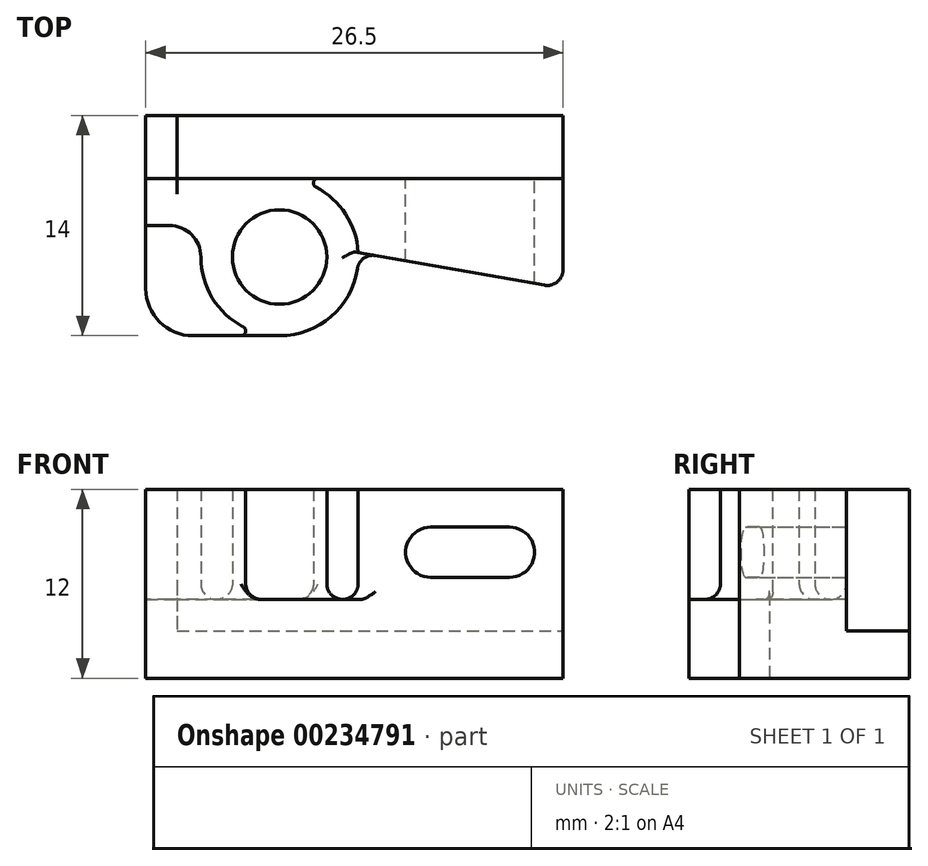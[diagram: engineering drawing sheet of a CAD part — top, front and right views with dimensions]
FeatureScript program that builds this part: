
annotation { "Feature Type Name" : "Feature", "Feature Type Description" : "" }
export const myFeature = defineFeature(function(context is Context, id is Id, definition is map)
    precondition{}
    {
        {
            var Q0;
            Q0=qCreatedBy(makeId("Top.planeOp"),FACE);
            var sketch = newSketch(context, id + "F0", { "sketchPlane" : qUnion([Q0])});
            skLineSegment(sketch, "E0", {"start": v(0, 5) * mm, "end": v(18, 5) * mm});
            skLineSegment(sketch, "E1", {"start": v(18, 5) * mm, "end": v(18, -2) * mm});
            skLineSegment(sketch, "E2", {"start": v(18, -2) * mm, "end": v(5, 0.3) * mm});
            skLineSegment(sketch, "E3", {"start": v(0, -5) * mm, "end": v(-5.5, -5) * mm});
            skLineSegment(sketch, "E4", {"start": v(-8.5, -2) * mm, "end": v(-8.5, 2) * mm});
            skLineSegment(sketch, "E5", {"start": v(-8.5, 2) * mm, "end": v(-7, 2) * mm});
            skCircle(sketch, "E6", {"center": v(0, 0) * mm, "radius": 3 * mm});
            skLineSegment(sketch, "E7", {"start": v(-8.5, 2) * mm, "end": v(-8.5, 9) * mm});
            skLineSegment(sketch, "E8", {"start": v(-8.5, 9) * mm, "end": v(18, 9) * mm});
            skLineSegment(sketch, "E9", {"start": v(18, 9) * mm, "end": v(18, 5) * mm});
            skLineSegment(sketch, "E10", {"start": v(0, 5) * mm, "end": v(-8.5, 5) * mm});
            skPoint(sketch, "E11.visualSharp", {"position": v(-8.5, -5) * mm});
            skArc(sketch, "E11.filletArc", {"start": v(-8.5, -2) * mm, "mid": v(-7.62, -4.12) * mm, "end": v(-5.5, -5) * mm});
            skArc(sketch, "E12", {"start": v(-5, 0) * mm, "mid": v(3.54, -3.54) * mm, "end": v(0, 5) * mm});
            skPoint(sketch, "E13.visualSharp", {"position": v(-4.58, 2) * mm});
            skArc(sketch, "E13.filletArc", {"start": v(-5, 0) * mm, "mid": v(-5.59, 1.41) * mm, "end": v(-7, 2) * mm});
            skLineSegment(sketch, "E14", {"start": v(-6.5, 5) * mm, "end": v(-6.5, 9) * mm});
            skSolve(sketch);
        }
        {
            var Q0;
            Q0=makeQuery(id+"F0.imprint","IMPRINT",FACE,{"disambiguationData":[TD([[makeQuery(id+"F0.imprint","IMPRINT",EDGE,{"derivedFrom":sQuery(id+"F0.wireOp",EDGE,"E0")}),1.0]])]});
            var Q1;
            {var subQ2=sQuery(id+"F0.wireOp",EDGE,"E5");Q1=makeQuery(id+"F0.imprint","IMPRINT",FACE,{"disambiguationData":[TD([[makeQuery(id+"F0.imprint","IMPRINT",EDGE,{"derivedFrom":subQ2}),1.0]])]});}
            var Q2;
            {var subQ0=sQuery(id+"F0.wireOp",EDGE,"E0");Q2=makeQuery(id+"F0.imprint","IMPRINT",FACE,{"disambiguationData":[TD([[makeQuery(id+"F0.imprint","IMPRINT",EDGE,{"derivedFrom":subQ0}),-1.0]])]});}
            var Q3;
            Q3=makeQuery(id+"F0.imprint","IMPRINT",FACE,{"disambiguationData":[TD([[makeQuery(id+"F0.imprint","IMPRINT",EDGE,{"derivedFrom":sQuery(id+"F0.wireOp",EDGE,"E6")}),1.0]])]});
            var Q4;
            {var subQ1=sQuery(id+"F0.wireOp",EDGE,"E3");Q4=makeQuery(id+"F0.imprint","IMPRINT",FACE,{"disambiguationData":[TD([[makeQuery(id+"F0.imprint","IMPRINT",EDGE,{"derivedFrom":subQ1}),-1.0]])]});}
            var Q5;
            {var subQ5=sQuery(id+"F0.wireOp",EDGE,"E14");Q5=makeQuery(id+"F0.imprint","IMPRINT",FACE,{"disambiguationData":[TD([[makeQuery(id+"F0.imprint","IMPRINT",EDGE,{"derivedFrom":subQ5}),1.0]])]});}
            extrude(context, id + "F1", {"entities" : qUnion([Q0, Q1, Q2, Q3, Q4, Q5]), "depth" : 3 * mm});
        }
        {
            var Q0;
            {var subQ0=sQuery(id+"F0.wireOp",EDGE,"E0");Q0=makeQuery(id+"F0.imprint","IMPRINT",FACE,{"disambiguationData":[TD([[makeQuery(id+"F0.imprint","IMPRINT",EDGE,{"derivedFrom":subQ0}),-1.0]])]});}
            var Q1;
            Q1=makeQuery(id+"F0.imprint","IMPRINT",FACE,{"disambiguationData":[TD([[makeQuery(id+"F0.imprint","IMPRINT",EDGE,{"derivedFrom":sQuery(id+"F0.wireOp",EDGE,"E6")}),1.0]])]});
            var Q2;
            {var subQ1=sQuery(id+"F0.wireOp",EDGE,"E3");Q2=makeQuery(id+"F0.imprint","IMPRINT",FACE,{"disambiguationData":[TD([[makeQuery(id+"F0.imprint","IMPRINT",EDGE,{"derivedFrom":subQ1}),-1.0]])]});}
            var Q3;
            {var subQ2=sQuery(id+"F0.wireOp",EDGE,"E5");Q3=makeQuery(id+"F0.imprint","IMPRINT",FACE,{"disambiguationData":[TD([[makeQuery(id+"F0.imprint","IMPRINT",EDGE,{"derivedFrom":subQ2}),1.0]])]});}
            var Q4;
            {var subQ5=sQuery(id+"F0.wireOp",EDGE,"E14");Q4=makeQuery(id+"F0.imprint","IMPRINT",FACE,{"disambiguationData":[TD([[makeQuery(id+"F0.imprint","IMPRINT",EDGE,{"derivedFrom":subQ5}),1.0]])]});}
            extrude(context, id + "F2", {"entities" : qUnion([Q0, Q1, Q2, Q3, Q4]), "operationType" : NewBodyOperationType.ADD, "depth" : 5 * mm});
        }
        {
            var Q0;
            {var subQ0=sQuery(id+"F0.wireOp",EDGE,"E0");Q0=makeQuery(id+"F0.imprint","IMPRINT",FACE,{"disambiguationData":[TD([[makeQuery(id+"F0.imprint","IMPRINT",EDGE,{"derivedFrom":subQ0}),-1.0]])]});}
            var Q1;
            Q1=makeQuery(id+"F0.imprint","IMPRINT",FACE,{"disambiguationData":[TD([[makeQuery(id+"F0.imprint","IMPRINT",EDGE,{"derivedFrom":sQuery(id+"F0.wireOp",EDGE,"E6")}),1.0]])]});
            var Q2;
            {var subQ1=sQuery(id+"F0.wireOp",EDGE,"E3");Q2=makeQuery(id+"F0.imprint","IMPRINT",FACE,{"disambiguationData":[TD([[makeQuery(id+"F0.imprint","IMPRINT",EDGE,{"derivedFrom":subQ1}),-1.0]])]});}
            var Q3;
            {var subQ5=sQuery(id+"F0.wireOp",EDGE,"E14");Q3=makeQuery(id+"F0.imprint","IMPRINT",FACE,{"disambiguationData":[TD([[makeQuery(id+"F0.imprint","IMPRINT",EDGE,{"derivedFrom":subQ5}),1.0]])]});}
            extrude(context, id + "F3", {"entities" : qUnion([Q0, Q1, Q2, Q3]), "operationType" : NewBodyOperationType.ADD, "depth" : 12 * mm});
        }
        {
            var Q0;
            Q0=makeQuery(id+"F3.opExtrude","SWEPT_EDGE",EDGE,{"disambiguationData":[OSD([sQuery(id+"F0.wireOp",EDGE,"E0"),sQuery(id+"F0.wireOp",EDGE,"E10"),sQuery(id+"F0.wireOp",EDGE,"E12")])]});
            var Q1;
            Q1=makeQuery(id+"F3.opExtrude","SWEPT_EDGE",EDGE,{"disambiguationData":[OSD([sQuery(id+"F0.wireOp",EDGE,"E3"),sQuery(id+"F0.wireOp",EDGE,"E12")])]});
            fillet(context, id + "F4", {"entities" : qUnion([Q0, Q1]), "radius" : 0.3 * mm, "tangentPropagation" : true, "allowEdgeOverflow" : false});
        }
        {
            var Q0;
            Q0=makeQuery(id+"F3.boolean.opBoolean","INTERSECT",EDGE,{"derivedFrom":[makeQuery(id+"F2.opExtrude","CAP_FACE",FACE,{"disambiguationData":[OSD([sQuery(id+"F0.wireOp",EDGE,"E0"),sQuery(id+"F0.wireOp",EDGE,"E1"),sQuery(id+"F0.wireOp",EDGE,"E2"),sQuery(id+"F0.wireOp",EDGE,"E3"),sQuery(id+"F0.wireOp",EDGE,"E4"),sQuery(id+"F0.wireOp",EDGE,"E7"),sQuery(id+"F0.wireOp",EDGE,"E10"),sQuery(id+"F0.wireOp",EDGE,"E11.filletArc"),sQuery(id+"F0.wireOp",EDGE,"E12")])],"isStart":false}),makeQuery(id+"F3.opExtrude","SWEPT_FACE",FACE,{"disambiguationData":[OSD([sQuery(id+"F0.wireOp",EDGE,"E6")])]})]});
            var Q1;
            {var subQ0=sQuery(id+"F0.wireOp",EDGE,"E12");var subQ1=sQuery(id+"F0.wireOp",EDGE,"E3");Q1=makeQuery(id+"F3.boolean.opBoolean","INTERSECT",EDGE,{"derivedFrom":[makeQuery(id+"F2.opExtrude","CAP_FACE",FACE,{"disambiguationData":[OSD([sQuery(id+"F0.wireOp",EDGE,"E0"),sQuery(id+"F0.wireOp",EDGE,"E1"),sQuery(id+"F0.wireOp",EDGE,"E2"),subQ1,sQuery(id+"F0.wireOp",EDGE,"E4"),sQuery(id+"F0.wireOp",EDGE,"E7"),sQuery(id+"F0.wireOp",EDGE,"E10"),sQuery(id+"F0.wireOp",EDGE,"E11.filletArc"),subQ0])],"isStart":false}),makeQuery(id+"F3.opExtrude","SWEPT_FACE",FACE,{"disambiguationData":[OSD([subQ0]),TDD([makeQuery(id+"F0.imprint","IMPRINT",EDGE,{"disambiguationData":[TD([[makeQuery(id+"F0.imprint","INTERSECT",VERTEX,{"derivedFrom":[subQ1,subQ0]}),1.0]])],"derivedFrom":subQ0})])]})]});}
            var Q2;
            {var subQ0=sQuery(id+"F0.wireOp",EDGE,"E12");var subQ1=sQuery(id+"F0.wireOp",EDGE,"E10");var subQ2=sQuery(id+"F0.wireOp",EDGE,"E0");var subQ3=sQuery(id+"F0.wireOp",EDGE,"E2");Q2=makeQuery(id+"F3.boolean.opBoolean","INTERSECT",EDGE,{"derivedFrom":[makeQuery(id+"F2.opExtrude","CAP_FACE",FACE,{"disambiguationData":[OSD([subQ2,sQuery(id+"F0.wireOp",EDGE,"E1"),subQ3,sQuery(id+"F0.wireOp",EDGE,"E3"),sQuery(id+"F0.wireOp",EDGE,"E4"),sQuery(id+"F0.wireOp",EDGE,"E7"),subQ1,sQuery(id+"F0.wireOp",EDGE,"E11.filletArc"),subQ0])],"isStart":false}),makeQuery(id+"F3.opExtrude","SWEPT_FACE",FACE,{"disambiguationData":[OSD([subQ0]),TDD([makeQuery(id+"F0.imprint","IMPRINT",EDGE,{"disambiguationData":[TD([[makeQuery(id+"F0.imprint","INTERSECT",VERTEX,{"derivedFrom":[subQ3,subQ0]}),-1.0]])],"derivedFrom":subQ0})])]})]});}
            var Q3;
            {var subQ0=sQuery(id+"F0.wireOp",EDGE,"E10");Q3=makeQuery(id+"F3.boolean.opBoolean","INTERSECT",EDGE,{"derivedFrom":[makeQuery(id+"F2.opExtrude","CAP_FACE",FACE,{"disambiguationData":[OSD([sQuery(id+"F0.wireOp",EDGE,"E0"),sQuery(id+"F0.wireOp",EDGE,"E1"),sQuery(id+"F0.wireOp",EDGE,"E2"),sQuery(id+"F0.wireOp",EDGE,"E3"),sQuery(id+"F0.wireOp",EDGE,"E4"),sQuery(id+"F0.wireOp",EDGE,"E7"),sQuery(id+"F0.wireOp",EDGE,"E8"),subQ0,sQuery(id+"F0.wireOp",EDGE,"E11.filletArc"),sQuery(id+"F0.wireOp",EDGE,"E12"),sQuery(id+"F0.wireOp",EDGE,"E14")])],"isStart":false}),makeQuery(id+"F3.opExtrude","SWEPT_FACE",FACE,{"disambiguationData":[OSD([subQ0])]})]});}
            fillet(context, id + "F5", {"entities" : qUnion([Q0, Q1, Q2, Q3]), "radius" : 1 * mm, "tangentPropagation" : true, "allowEdgeOverflow" : false});
        }
        {
            var Q0;
            {var subQ0=sQuery(id+"F0.wireOp",EDGE,"E12");var subQ1=sQuery(id+"F0.wireOp",EDGE,"E2");Q0=makeQuery(id+"F2.boolean.opBoolean","MERGE",EDGE,{"derivedFrom":[makeQuery(id+"F1.opExtrude","SWEPT_EDGE",EDGE,{"disambiguationData":[OSD([subQ1,subQ0])]}),makeQuery(id+"F2.opExtrude","SWEPT_EDGE",EDGE,{"disambiguationData":[OSD([subQ1,subQ0])]})]});}
            var Q1;
            {var subQ0=sQuery(id+"F0.wireOp",EDGE,"E12");var subQ1=sQuery(id+"F0.wireOp",EDGE,"E3");Q1=makeQuery(id+"F2.boolean.opBoolean","MERGE",EDGE,{"derivedFrom":[makeQuery(id+"F1.opExtrude","SWEPT_EDGE",EDGE,{"disambiguationData":[OSD([subQ1,subQ0])]}),makeQuery(id+"F2.opExtrude","SWEPT_EDGE",EDGE,{"disambiguationData":[OSD([subQ1,subQ0])]})]});}
            var Q2;
            {var subQ0=sQuery(id+"F0.wireOp",EDGE,"E2");var subQ1=sQuery(id+"F0.wireOp",EDGE,"E1");Q2=makeQuery(id+"F3.boolean.opBoolean","MERGE",EDGE,{"derivedFrom":[makeQuery(id+"F2.boolean.opBoolean","MERGE",EDGE,{"derivedFrom":[makeQuery(id+"F1.opExtrude","SWEPT_EDGE",EDGE,{"disambiguationData":[OSD([subQ1,subQ0])]}),makeQuery(id+"F2.opExtrude","SWEPT_EDGE",EDGE,{"disambiguationData":[OSD([subQ1,subQ0])]})]}),makeQuery(id+"F3.opExtrude","SWEPT_EDGE",EDGE,{"disambiguationData":[OSD([subQ1,subQ0])]})]});}
            fillet(context, id + "F6", {"entities" : qUnion([Q0, Q1, Q2]), "radius" : 1 * mm, "tangentPropagation" : true, "allowEdgeOverflow" : false});
        }
        {
            var Q0;
            Q0=makeQuery(id+"F5.opFillet","TWEAK_EDGE",EDGE,{"derivedFrom":[makeQuery(id+"F2.opExtrude","CAP_VERTEX",VERTEX,{"disambiguationData":[OSD([sQuery(id+"F0.wireOp",EDGE,"E3"),sQuery(id+"F0.wireOp",EDGE,"E12")])],"isStart":false})]});
            var Q1;
            Q1=makeQuery(id+"F5.opFillet","TWEAK_EDGE",EDGE,{"derivedFrom":[makeQuery(id+"F2.opExtrude","CAP_VERTEX",VERTEX,{"disambiguationData":[OSD([sQuery(id+"F0.wireOp",EDGE,"E2"),sQuery(id+"F0.wireOp",EDGE,"E12")])],"isStart":false})]});
            fillet(context, id + "F7", {"entities" : qUnion([Q0, Q1]), "radius" : 0.5 * mm, "tangentPropagation" : true, "allowEdgeOverflow" : false});
        }
        {
            var Q0;
            {var subQ0=sQuery(id+"F0.wireOp",EDGE,"E0");var subQ1=sQuery(id+"F0.wireOp",EDGE,"E10");Q0=makeQuery(id+"F3.boolean.opBoolean","MERGE",FACE,{"derivedFrom":[makeQuery(id+"F2.boolean.opBoolean","MERGE",FACE,{"derivedFrom":[makeQuery(id+"F1.opExtrude","SWEPT_FACE",FACE,{"disambiguationData":[OSD([subQ1])]}),makeQuery(id+"F2.opExtrude","SWEPT_FACE",FACE,{"disambiguationData":[OSD([subQ0,subQ1])]})]}),makeQuery(id+"F3.opExtrude","SWEPT_FACE",FACE,{"disambiguationData":[OSD([subQ0])]})]});}
            var sketch = newSketch(context, id + "F8", { "sketchPlane" : qUnion([Q0])});
            skLineSegment(sketch, "E15.bottom", {"start": v(-14.6, 6.4) * mm, "end": v(-9.6, 6.4) * mm});
            skLineSegment(sketch, "E15.top", {"start": v(-14.6, 9.6) * mm, "end": v(-9.6, 9.6) * mm});
            skArc(sketch, "E16", {"start": v(-9.6, 9.6) * mm, "mid": v(-8, 8) * mm, "end": v(-9.6, 6.4) * mm});
            skArc(sketch, "E17.trimOffspring", {"start": v(-14.6, 6.4) * mm, "mid": v(-16.2, 8) * mm, "end": v(-14.6, 9.6) * mm});
            skSolve(sketch);
        }
        {
            var Q0;
            {var subQ1=sQuery(id+"F8.wireOp",EDGE,"E15.bottom");Q0=makeQuery(id+"F8.imprint","IMPRINT",FACE,{"disambiguationData":[TD([[makeQuery(id+"F8.imprint","IMPRINT",EDGE,{"derivedFrom":subQ1}),1.0]])]});}
            extrude(context, id + "F9", {"entities" : qUnion([Q0]), "operationType" : NewBodyOperationType.REMOVE, "oppositeDirection" : true, "depth" : 7 * mm});
        }
    });
